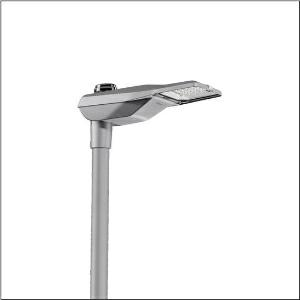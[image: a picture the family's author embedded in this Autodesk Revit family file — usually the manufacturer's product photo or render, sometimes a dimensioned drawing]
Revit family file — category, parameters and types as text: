
# Revit family: streetlight_sl_21_micro___stw1_0a_5xe5e47n08db_5020
name_source: partatom
category: Lighting Fixtures
units: mm (PartAtom-declared; Revit-internal decimal feet)

## family parameters
Cut with Voids When Loaded = No
Host = Face
Light Source = No
Part Type = Normal
Room Calculation Point = No
Round Connector Dimension = Use Diameter
Shared = No

## types (1)
- --- (1 x LED, 5320 lm, 39.1 W, 4000K)
    Apparent Load = 39 VA
    CIE Flux Codes = 38 75 98 100 100
    Color Rendering = 70
    Color Temperature = 4000K
    Default Elevation = 1800 mm
    Description = Streetlight SL 21 micro, mast luminaire, primary light control with lens, of PMMA, primary optical cover: cover, of toughened safety glass, transparent, light distribution: STW1.0a, light emission: direct distribution, primary light characteristic: asymmetric, installation type: post-top, LED, 3G 1.5mm², High Power LED, rated luminous flux: 5.320lm, luminous efficacy: 136lm/W, light colour: 740, colour temperature: 4000K, control: overheat protection, pre-setting: linear dimming characteristic, constant luminous flux control, time-dependent luminous flux control, flexible luminous flux parameterisation, mains connection: 230..240V, AC, 50/60Hz, connection cable pre-assembled, cable length: 6,5m, wiring characteristics: H07RN-F, start of lifetime: 39W, end of service life: 41W, reduction: 18W, luminaire housing, of diecast aluminium (EN AC-44300), powder-coated, Siteco® metallic grey (DB 702S), corrosivity category C5 mid according to DIN EN ISO 12944, multi-level sealing system, sealing non-destructively replaceable, inclination adjustable: 0°, 5°, 10°, 15°, length: 528mm, width: 235mm, height: 110mm, spigot size: 76/60mm (post-top), protection rating (complete): IP66, insulation class (complete): insulation class I (protective earthing), certification: CE, ENEC, ENEC+, VDE, impact resistance: IK09, permissible operating ambient temperature for outdoor applications: -40..+50°C, standard-compliant lighting for roads and squares, packaging unit: 1 piece

Light Distribution: STW1.0a
    Height = 110 mm
    Lamp = 1 x LED
    Lamp Light Flux = 5320 lm
    Lamp Power = 39.1 W
    Lamp count = 1
    Length = 528 mm
    Luminous efficacy = 136 lm/W
    Manufacturer = Siteco
    ModVariant = No
    Model = 5XE5E47N08DB
    Number of Poles = 1
    OnlyDefault = Yes
    Power Factor = 1
    Product Name = Streetlight SL 21 micro | STW1.0a
    Product group = mast luminaire | pylon top
    ProductGroupID = 6100
    Protection Class = Protection class I
    Protection Degree = IP 66
    RLX_Detail_Level = 1
    RLX_Emergency_Light_Flux = 0 lm
    RLX_Emergency_Type = 0
    RLX_Emergency_Type_DB = No
    RlxData = <blob elided: 98833 chars, md5=25717666>
    Socket = socket
    Standby Power = 0 W
    System Light Flux = 5320 lm
    System Power = 39 W
    Type Comments = factory setting: luminous flux: 100 % | dim-lin: 254 | 765 mA
    Type Image = l_1294375.jpg
    URL = http://relux.com
    VarID = @adj_105557
    Voltage = 0 V
    Weight = 0.00 kg
    Width = 235 mm

## geometry (parser evidence)
native form markers: Blend x4, Sweep x9
no freeform markers — native parametric forms only
